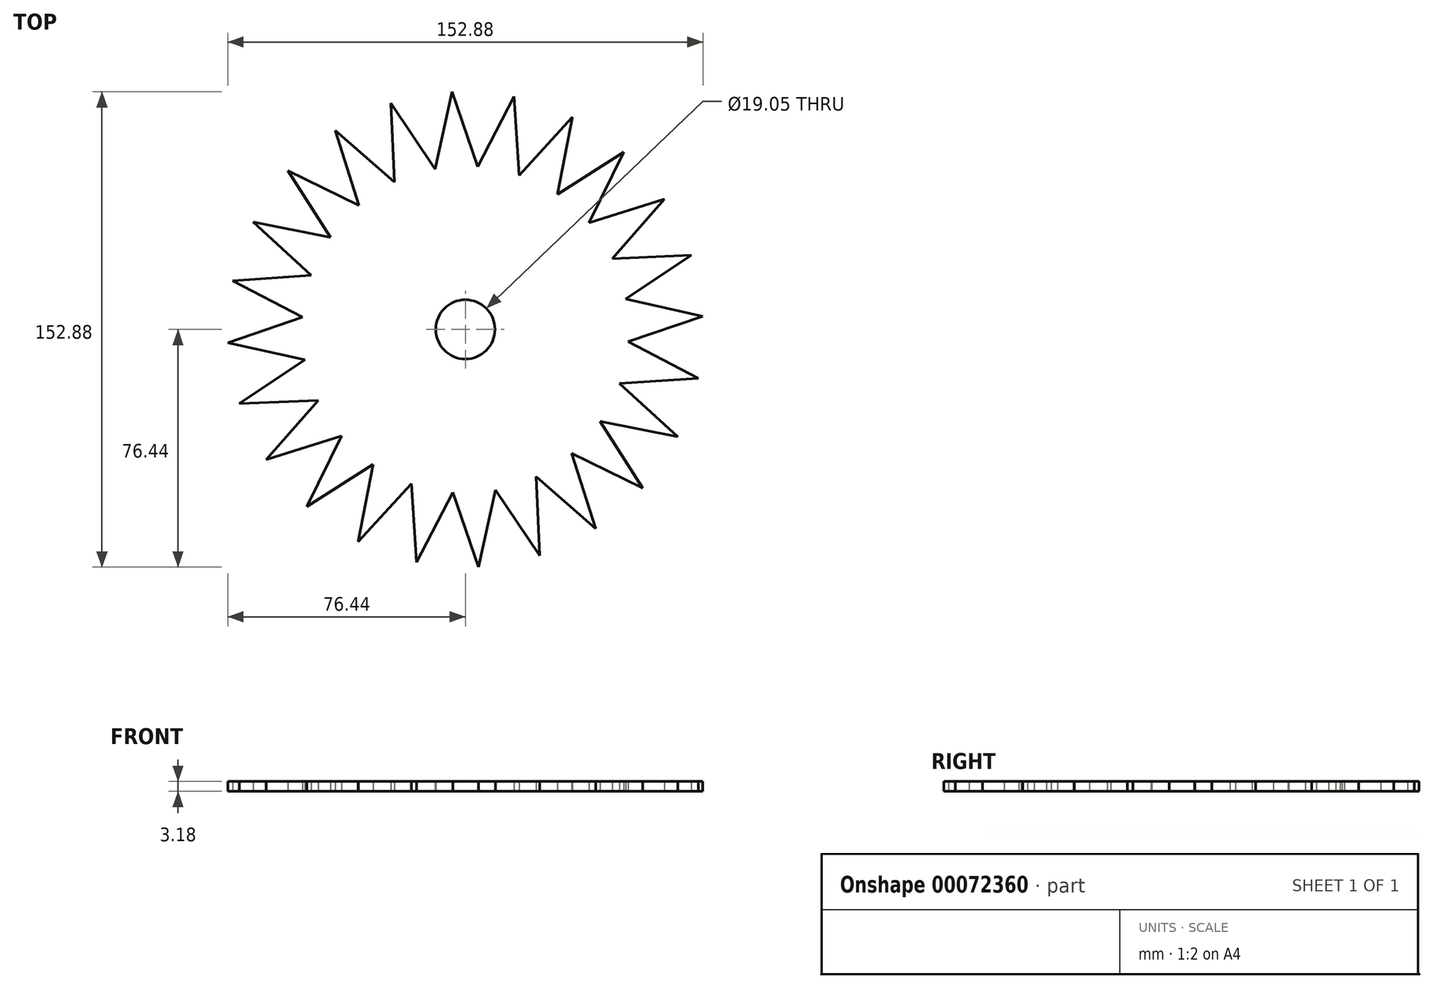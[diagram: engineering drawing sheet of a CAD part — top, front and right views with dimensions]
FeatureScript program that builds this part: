
annotation { "Feature Type Name" : "Feature", "Feature Type Description" : "" }
export const myFeature = defineFeature(function(context is Context, id is Id, definition is map)
    precondition{}
    {
        {
            var Q0;
            Q0=qCreatedBy(makeId("Top.planeOp"),FACE);
            var sketch = newSketch(context, id + "F0", { "sketchPlane" : qUnion([Q0])});
            skLineSegment(sketch, "E0", {"start": v(17.38, 49.6) * mm, "end": v(34.53, 68.33) * mm});
            skLineSegment(sketch, "E1", {"start": v(34.53, 68.33) * mm, "end": v(29.62, 43.4) * mm});
            skLineSegment(sketch, "E2.1.0", {"start": v(3.95, 52.4) * mm, "end": v(15.67, 74.94) * mm});
            skLineSegment(sketch, "E2.1.1", {"start": v(15.67, 74.94) * mm, "end": v(17.38, 49.6) * mm});
            skLineSegment(sketch, "E2.2.0", {"start": v(-9.75, 51.64) * mm, "end": v(-4.26, 76.44) * mm});
            skLineSegment(sketch, "E2.2.1", {"start": v(-4.26, 76.44) * mm, "end": v(3.95, 52.4) * mm});
            skLineSegment(sketch, "E2.3.0", {"start": v(-22.78, 47.35) * mm, "end": v(-23.9, 72.73) * mm});
            skLineSegment(sketch, "E2.3.1", {"start": v(-23.9, 72.73) * mm, "end": v(-9.75, 51.64) * mm});
            skLineSegment(sketch, "E2.4.0", {"start": v(-34.26, 39.84) * mm, "end": v(-41.9, 64.07) * mm});
            skLineSegment(sketch, "E2.4.1", {"start": v(-41.9, 64.07) * mm, "end": v(-22.78, 47.35) * mm});
            skLineSegment(sketch, "E2.5.0", {"start": v(-43.4, 29.62) * mm, "end": v(-57.06, 51.04) * mm});
            skLineSegment(sketch, "E2.5.1", {"start": v(-57.06, 51.04) * mm, "end": v(-34.26, 39.84) * mm});
            skLineSegment(sketch, "E2.6.0", {"start": v(-49.6, 17.38) * mm, "end": v(-68.33, 34.53) * mm});
            skLineSegment(sketch, "E2.6.1", {"start": v(-68.33, 34.53) * mm, "end": v(-43.4, 29.62) * mm});
            skLineSegment(sketch, "E2.7.0", {"start": v(-52.4, 3.95) * mm, "end": v(-74.94, 15.67) * mm});
            skLineSegment(sketch, "E2.7.1", {"start": v(-74.94, 15.67) * mm, "end": v(-49.6, 17.38) * mm});
            skLineSegment(sketch, "E2.8.0", {"start": v(-51.64, -9.75) * mm, "end": v(-76.44, -4.26) * mm});
            skLineSegment(sketch, "E2.8.1", {"start": v(-76.44, -4.26) * mm, "end": v(-52.4, 3.95) * mm});
            skLineSegment(sketch, "E2.9.0", {"start": v(-47.35, -22.78) * mm, "end": v(-72.73, -23.9) * mm});
            skLineSegment(sketch, "E2.9.1", {"start": v(-72.73, -23.9) * mm, "end": v(-51.64, -9.75) * mm});
            skLineSegment(sketch, "E2.10.0", {"start": v(-39.84, -34.26) * mm, "end": v(-64.07, -41.9) * mm});
            skLineSegment(sketch, "E2.10.1", {"start": v(-64.07, -41.9) * mm, "end": v(-47.35, -22.78) * mm});
            skLineSegment(sketch, "E2.11.0", {"start": v(-29.62, -43.4) * mm, "end": v(-51.04, -57.06) * mm});
            skLineSegment(sketch, "E2.11.1", {"start": v(-51.04, -57.06) * mm, "end": v(-39.84, -34.26) * mm});
            skLineSegment(sketch, "E2.12.0", {"start": v(-17.38, -49.6) * mm, "end": v(-34.53, -68.33) * mm});
            skLineSegment(sketch, "E2.12.1", {"start": v(-34.53, -68.33) * mm, "end": v(-29.62, -43.4) * mm});
            skLineSegment(sketch, "E2.13.0", {"start": v(-3.95, -52.4) * mm, "end": v(-15.67, -74.94) * mm});
            skLineSegment(sketch, "E2.13.1", {"start": v(-15.67, -74.94) * mm, "end": v(-17.38, -49.6) * mm});
            skLineSegment(sketch, "E2.14.0", {"start": v(9.75, -51.64) * mm, "end": v(4.26, -76.44) * mm});
            skLineSegment(sketch, "E2.14.1", {"start": v(4.26, -76.44) * mm, "end": v(-3.95, -52.4) * mm});
            skLineSegment(sketch, "E2.15.0", {"start": v(22.78, -47.35) * mm, "end": v(23.9, -72.73) * mm});
            skLineSegment(sketch, "E2.15.1", {"start": v(23.9, -72.73) * mm, "end": v(9.75, -51.64) * mm});
            skLineSegment(sketch, "E2.16.0", {"start": v(34.26, -39.84) * mm, "end": v(41.9, -64.07) * mm});
            skLineSegment(sketch, "E2.16.1", {"start": v(41.9, -64.07) * mm, "end": v(22.78, -47.35) * mm});
            skLineSegment(sketch, "E2.17.0", {"start": v(43.4, -29.62) * mm, "end": v(57.06, -51.04) * mm});
            skLineSegment(sketch, "E2.17.1", {"start": v(57.06, -51.04) * mm, "end": v(34.26, -39.84) * mm});
            skLineSegment(sketch, "E2.18.0", {"start": v(49.6, -17.38) * mm, "end": v(68.33, -34.53) * mm});
            skLineSegment(sketch, "E2.18.1", {"start": v(68.33, -34.53) * mm, "end": v(43.4, -29.62) * mm});
            skLineSegment(sketch, "E2.19.0", {"start": v(52.4, -3.95) * mm, "end": v(74.94, -15.67) * mm});
            skLineSegment(sketch, "E2.19.1", {"start": v(74.94, -15.67) * mm, "end": v(49.6, -17.38) * mm});
            skLineSegment(sketch, "E2.20.0", {"start": v(51.64, 9.75) * mm, "end": v(76.44, 4.26) * mm});
            skLineSegment(sketch, "E2.20.1", {"start": v(76.44, 4.26) * mm, "end": v(52.4, -3.95) * mm});
            skLineSegment(sketch, "E2.21.0", {"start": v(47.35, 22.78) * mm, "end": v(72.73, 23.9) * mm});
            skLineSegment(sketch, "E2.21.1", {"start": v(72.73, 23.9) * mm, "end": v(51.64, 9.75) * mm});
            skLineSegment(sketch, "E2.22.0", {"start": v(39.84, 34.26) * mm, "end": v(64.07, 41.9) * mm});
            skLineSegment(sketch, "E2.22.1", {"start": v(64.07, 41.9) * mm, "end": v(47.35, 22.78) * mm});
            skLineSegment(sketch, "E2.23.0", {"start": v(29.62, 43.4) * mm, "end": v(51.04, 57.06) * mm});
            skLineSegment(sketch, "E2.23.1", {"start": v(51.04, 57.06) * mm, "end": v(39.84, 34.26) * mm});
            skPoint(sketch, "E2.center", {"position": v(0, 0) * mm});
            skCircle(sketch, "E3", {"center": v(0, 0) * mm, "radius": 9.53 * mm});
            skSolve(sketch);
        }
        {
            var Q0;
            Q0=makeQuery(id+"F0.imprint","IMPRINT",FACE,{"disambiguationData":[TD([[makeQuery(id+"F0.imprint","IMPRINT",EDGE,{"derivedFrom":sQuery(id+"F0.wireOp",EDGE,"E0")}),-1.0]])]});
            extrude(context, id + "F1", {"entities" : qUnion([Q0]), "depth" : 3.17 * mm});
        }
    });
